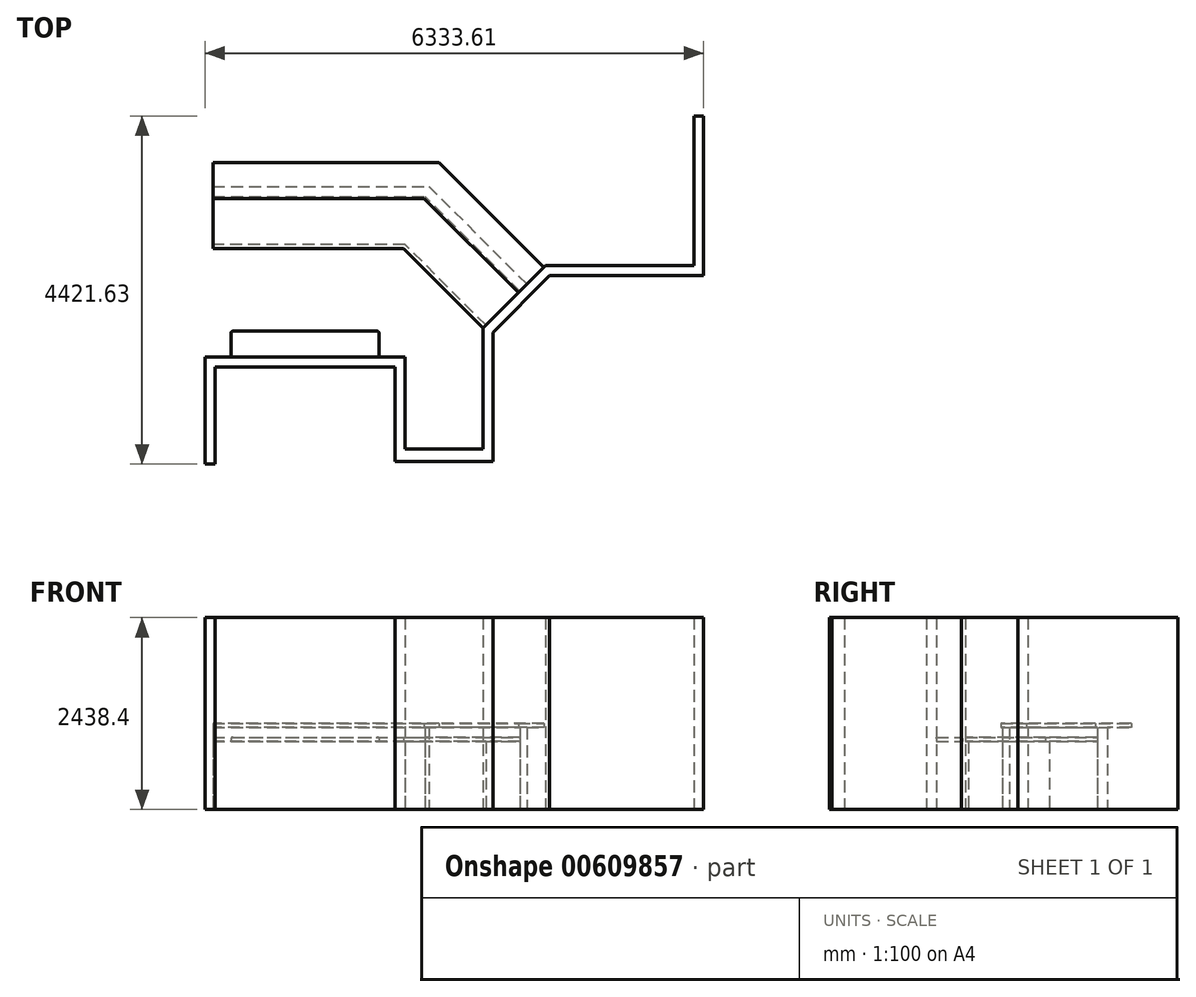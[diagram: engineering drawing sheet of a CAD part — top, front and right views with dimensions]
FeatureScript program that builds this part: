
annotation { "Feature Type Name" : "Feature", "Feature Type Description" : "" }
export const myFeature = defineFeature(function(context is Context, id is Id, definition is map)
    precondition{}
    {
        {
            var Q0;
            Q0=qCreatedBy(makeId("Top.planeOp"),FACE);
            var sketch = newSketch(context, id + "F0", { "sketchPlane" : qUnion([Q0])});
            skLineSegment(sketch, "E0", {"start": v(-1243.02, 0) * mm, "end": v(1296.98, 0) * mm});
            skLineSegment(sketch, "E1", {"start": v(1296.98, 0) * mm, "end": v(1296.98, -1168.4) * mm});
            skLineSegment(sketch, "E2", {"start": v(1296.98, -1168.4) * mm, "end": v(2287.58, -1168.4) * mm});
            skLineSegment(sketch, "E3", {"start": v(2287.58, -1168.4) * mm, "end": v(2287.58, 368.3) * mm});
            skLineSegment(sketch, "E4", {"start": v(2287.58, 368.3) * mm, "end": v(3082.33, 1163.05) * mm});
            skLineSegment(sketch, "E5", {"start": v(3082.33, 1163.05) * mm, "end": v(4967.08, 1163.05) * mm});
            skLineSegment(sketch, "E6", {"start": v(4967.08, 3063.83) * mm, "end": v(4967.08, 1163.05) * mm});
            skLineSegment(sketch, "E7", {"start": v(-1243.02, 0) * mm, "end": v(-1243.02, -1357.8) * mm});
            skLineSegment(sketch, "E8.bottom", {"start": v(-887.42, 0) * mm, "end": v(941.38, 0) * mm});
            skLineSegment(sketch, "E8.top", {"start": v(-887.42, 304.8) * mm, "end": v(941.38, 304.8) * mm});
            skLineSegment(sketch, "E8.left", {"start": v(-887.42, 0) * mm, "end": v(-887.42, 304.8) * mm});
            skLineSegment(sketch, "E8.right", {"start": v(941.38, 0) * mm, "end": v(941.38, 304.8) * mm});
            skLineSegment(sketch, "E9", {"start": v(2324.68, 405.4) * mm, "end": v(1296.98, 1433.1) * mm});
            skLineSegment(sketch, "E10", {"start": v(2755.73, 836.45) * mm, "end": v(1549.48, 2042.7) * mm});
            skLineSegment(sketch, "E11", {"start": v(1296.98, 0) * mm, "end": v(1296.98, 1433.1) * mm, "construction": true});
            skLineSegment(sketch, "E12", {"start": v(1296.98, 1433.1) * mm, "end": v(-1141.42, 1433.1) * mm});
            skLineSegment(sketch, "E13", {"start": v(-1141.42, 2042.7) * mm, "end": v(-1141.42, 1433.1) * mm});
            skLineSegment(sketch, "E14", {"start": v(-1141.42, 2042.7) * mm, "end": v(1549.48, 2042.7) * mm});
            skLineSegment(sketch, "E15", {"start": v(2845.53, 926.25) * mm, "end": v(1602.09, 2169.7) * mm});
            skLineSegment(sketch, "E16", {"start": v(-1141.42, 2169.7) * mm, "end": v(1602.09, 2169.7) * mm});
            skLineSegment(sketch, "E17", {"start": v(-1141.42, 2169.7) * mm, "end": v(-1141.42, 2042.7) * mm});
            skLineSegment(sketch, "E18", {"start": v(3061.06, 1141.78) * mm, "end": v(1728.34, 2474.5) * mm});
            skLineSegment(sketch, "E19", {"start": v(1728.34, 2474.5) * mm, "end": v(-1141.42, 2474.5) * mm});
            skLineSegment(sketch, "E20", {"start": v(-1141.42, 2474.5) * mm, "end": v(-1141.42, 2169.7) * mm});
            skLineSegment(sketch, "E21", {"start": v(4967.08, 3063.83) * mm, "end": v(5090.59, 3063.83) * mm});
            skLineSegment(sketch, "E22", {"start": v(5090.59, 3063.83) * mm, "end": v(5090.59, 1036.05) * mm});
            skLineSegment(sketch, "E23", {"start": v(5090.59, 1036.05) * mm, "end": v(3134.94, 1036.05) * mm});
            skLineSegment(sketch, "E24", {"start": v(3134.94, 1036.05) * mm, "end": v(2414.58, 315.7) * mm});
            skLineSegment(sketch, "E25", {"start": v(2414.58, 315.7) * mm, "end": v(2414.58, -1328.1) * mm});
            skLineSegment(sketch, "E26", {"start": v(2414.58, -1328.1) * mm, "end": v(1169.98, -1328.1) * mm});
            skLineSegment(sketch, "E27", {"start": v(1169.98, -1328.1) * mm, "end": v(1169.98, -127) * mm});
            skLineSegment(sketch, "E28", {"start": v(1169.98, -127) * mm, "end": v(-1116.02, -127) * mm});
            skLineSegment(sketch, "E29", {"start": v(-1116.02, -127) * mm, "end": v(-1116.02, -1357.8) * mm});
            skLineSegment(sketch, "E30", {"start": v(-1116.02, -1357.8) * mm, "end": v(-1243.02, -1357.8) * mm});
            skSolve(sketch);
        }
        {
            var Q0;
            {var subQ1=sQuery(id+"F0.wireOp",EDGE,"E9");Q0=makeQuery(id+"F0.imprint","IMPRINT",FACE,{"disambiguationData":[TD([[makeQuery(id+"F0.imprint","IMPRINT",EDGE,{"derivedFrom":subQ1}),-1.0]])]});}
            var Q1;
            Q1=makeQuery(id+"F0.imprint","IMPRINT",FACE,{"disambiguationData":[TD([[makeQuery(id+"F0.imprint","IMPRINT",EDGE,{"derivedFrom":sQuery(id+"F0.wireOp",EDGE,"E8.bottom")}),1.0]])]});
            extrude(context, id + "F1", {"entities" : qUnion([Q0, Q1]), "depth" : 863.6 * mm, "offsetDistance" : 25.4 * mm});
        }
        {
            var Q0;
            {var subQ3=sQuery(id+"F0.wireOp",EDGE,"E1");Q0=makeQuery(id+"F0.imprint","IMPRINT",FACE,{"disambiguationData":[TD([[makeQuery(id+"F0.imprint","IMPRINT",EDGE,{"derivedFrom":subQ3}),-1.0]])]});}
            extrude(context, id + "F2", {"entities" : qUnion([Q0]), "depth" : 2438.4 * mm, "offsetDistance" : 25.4 * mm});
        }
        {
            var Q0;
            {var subQ0=sQuery(id+"F0.wireOp",EDGE,"E10");Q0=makeQuery(id+"F0.imprint","IMPRINT",FACE,{"disambiguationData":[TD([[makeQuery(id+"F0.imprint","IMPRINT",EDGE,{"derivedFrom":subQ0}),-1.0]])]});}
            extrude(context, id + "F3", {"entities" : qUnion([Q0]), "depth" : 1041.4 * mm, "offsetDistance" : 25.4 * mm});
        }
        {
            var Q0;
            Q0=makeQuery(id+"F3.opExtrude","CAP_FACE",FACE,{"disambiguationData":[OSD([sQuery(id+"F0.wireOp",EDGE,"E4"),sQuery(id+"F0.wireOp",EDGE,"E10"),sQuery(id+"F0.wireOp",EDGE,"E14"),sQuery(id+"F0.wireOp",EDGE,"E15"),sQuery(id+"F0.wireOp",EDGE,"E16"),sQuery(id+"F0.wireOp",EDGE,"E17")])],"isStart":false});
            var sketch = newSketch(context, id + "F4", { "sketchPlane" : qUnion([Q0])});
            skLineSegment(sketch, "E31", {"start": v(2737.77, 818.5) * mm, "end": v(3061.06, 1141.78) * mm});
            skLineSegment(sketch, "E32", {"start": v(3061.06, 1141.78) * mm, "end": v(1728.34, 2474.5) * mm});
            skLineSegment(sketch, "E33", {"start": v(1728.34, 2474.5) * mm, "end": v(-1141.42, 2474.5) * mm});
            skLineSegment(sketch, "E34", {"start": v(-1141.42, 2474.5) * mm, "end": v(-1141.42, 2017.3) * mm});
            skLineSegment(sketch, "E35", {"start": v(-1141.42, 2017.3) * mm, "end": v(1538.96, 2017.3) * mm});
            skLineSegment(sketch, "E36", {"start": v(1538.96, 2017.3) * mm, "end": v(2737.77, 818.5) * mm});
            skSolve(sketch);
        }
        {
            var Q0;
            Q0 = qSketchRegion(id + "F4", true);
            extrude(context, id + "F5", {"entities" : qUnion([Q0]), "operationType" : NewBodyOperationType.ADD, "depth" : 50.8 * mm, "offsetDistance" : 25.4 * mm});
        }
        {
            var Q0;
            Q0=makeQuery(id+"F1.opExtrude","CAP_FACE",FACE,{"disambiguationData":[OSD([sQuery(id+"F0.wireOp",EDGE,"E4"),sQuery(id+"F0.wireOp",EDGE,"E9"),sQuery(id+"F0.wireOp",EDGE,"E10"),sQuery(id+"F0.wireOp",EDGE,"E12"),sQuery(id+"F0.wireOp",EDGE,"E13"),sQuery(id+"F0.wireOp",EDGE,"E14")])],"isStart":false});
            var sketch = newSketch(context, id + "F6", { "sketchPlane" : qUnion([Q0])});
            skLineSegment(sketch, "E37", {"start": v(2755.73, 836.45) * mm, "end": v(1549.48, 2042.7) * mm});
            skLineSegment(sketch, "E38", {"start": v(1549.48, 2042.7) * mm, "end": v(-1141.42, 2042.7) * mm});
            skLineSegment(sketch, "E39", {"start": v(-1141.42, 2042.7) * mm, "end": v(-1141.42, 1382.3) * mm});
            skLineSegment(sketch, "E40", {"start": v(-1141.42, 1382.3) * mm, "end": v(1275.94, 1382.3) * mm});
            skLineSegment(sketch, "E41", {"start": v(1275.94, 1382.3) * mm, "end": v(2288.76, 369.48) * mm});
            skLineSegment(sketch, "E42", {"start": v(2755.73, 836.45) * mm, "end": v(2288.76, 369.48) * mm});
            skLineSegment(sketch, "E43.bottom", {"start": v(-912.82, 0) * mm, "end": v(966.78, 0) * mm});
            skLineSegment(sketch, "E43.top", {"start": v(-912.82, 330.2) * mm, "end": v(966.78, 330.2) * mm});
            skLineSegment(sketch, "E43.left", {"start": v(-912.82, 0) * mm, "end": v(-912.82, 330.2) * mm});
            skLineSegment(sketch, "E43.right", {"start": v(966.78, 0) * mm, "end": v(966.78, 330.2) * mm});
            skSolve(sketch);
        }
        {
            var Q0;
            Q0=makeQuery(id+"F6.imprint","IMPRINT",FACE,{"disambiguationData":[TD([[makeQuery(id+"F6.imprint","IMPRINT",EDGE,{"derivedFrom":sQuery(id+"F6.wireOp",EDGE,"E43.bottom")}),1.0]])]});
            var Q1;
            {var subQ2=sQuery(id+"F6.wireOp",EDGE,"E37");Q1=makeQuery(id+"F6.imprint","IMPRINT",FACE,{"disambiguationData":[TD([[makeQuery(id+"F6.imprint","IMPRINT",EDGE,{"derivedFrom":subQ2}),1.0]])]});}
            var Q2;
            {var subQ3=sQuery(id+"F6.wireOp",EDGE,"E40");Q2=makeQuery(id+"F6.imprint","IMPRINT",FACE,{"disambiguationData":[TD([[makeQuery(id+"F6.imprint","IMPRINT",EDGE,{"derivedFrom":subQ3}),1.0]])]});}
            var Q3;
            Q3=sQuery(id+"F6.wireOp",EDGE,"E43.left");
            var Q4;
            Q4=sQuery(id+"F6.wireOp",EDGE,"E41");
            var Q5;
            Q5=sQuery(id+"F6.wireOp",EDGE,"E43.top");
            var Q6;
            Q6=sQuery(id+"F6.wireOp",EDGE,"E43.right");
            var Q7;
            Q7=sQuery(id+"F6.wireOp",EDGE,"E40");
            var Q8;
            Q8=sQuery(id+"F6.wireOp",EDGE,"E39");
            extrude(context, id + "F7", {"entities" : qUnion([Q0, Q1, Q2]), "surfaceEntities" : qUnion([Q3, Q4, Q5, Q6, Q7, Q8]), "depth" : 50.8 * mm, "offsetDistance" : 25.4 * mm});
        }
        {
            var Q0;
            Q0=makeQuery(id+"F7.opExtrude","SWEPT_EDGE",EDGE,{"disambiguationData":[OSD([sQuery(id+"F6.wireOp",EDGE,"E43.top"),sQuery(id+"F6.wireOp",EDGE,"E43.left")])]});
            var Q1;
            Q1=makeQuery(id+"F7.opExtrude","SWEPT_EDGE",EDGE,{"disambiguationData":[OSD([sQuery(id+"F6.wireOp",EDGE,"E43.top"),sQuery(id+"F6.wireOp",EDGE,"E43.right")])]});
            fillet(context, id + "F8", {"entities" : qUnion([Q0, Q1]), "radius" : 25.4 * mm, "tangentPropagation" : true, "allowEdgeOverflow" : false});
        }
        {
            var Q0;
            Q0=makeQuery(id+"F7.opExtrude","CAP_EDGE",EDGE,{"disambiguationData":[OSD([sQuery(id+"F6.wireOp",EDGE,"E43.right")])],"isStart":false});
            var Q1;
            Q1=makeQuery(id+"F7.opExtrude","CAP_EDGE",EDGE,{"disambiguationData":[OSD([sQuery(id+"F6.wireOp",EDGE,"E43.top")])],"isStart":false});
            fillet(context, id + "F9", {"entities" : qUnion([Q0, Q1]), "radius" : 12.7 * mm, "tangentPropagation" : true, "allowEdgeOverflow" : false});
        }
    });
